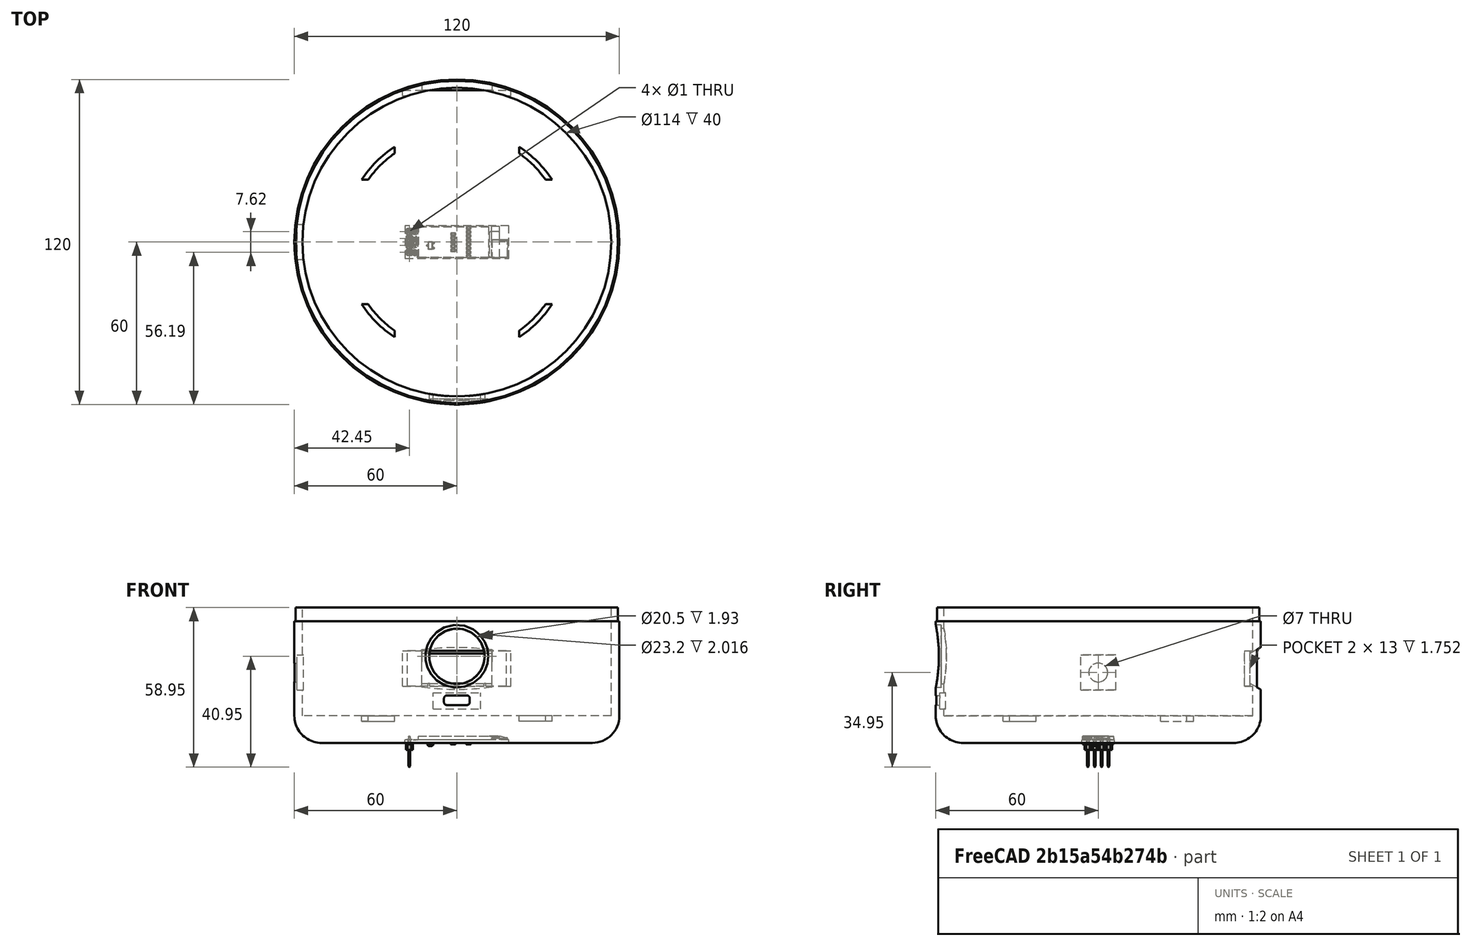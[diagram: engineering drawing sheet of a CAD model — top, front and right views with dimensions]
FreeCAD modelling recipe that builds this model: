
FCSTD DOCUMENT  (FreeCAD 0.18R4 (GitTag))
Label: 1
License: All rights reserved
LicenseURL: http://en.wikipedia.org/wiki/All_rights_reserved
objects: Part::Cut×18, Part::Feature×16, Part::Box×11, Part::Cylinder×10, Part::Fillet×2, Part::Fuse×2, App::Part×1
note: 59 computed .brp shape members not serialized (recipe doc carries the construction recipe); baked Part::Feature solids carry a one-line shape summary decoded from their .brp

FEATURE [Part::Cylinder] Cylinder  label="Base"
  Angle = 360
  AttacherType = Attacher::AttachEngine3D
  Height = 50
  Radius = 60
FEATURE [Part::Cylinder] Cylinder001  label="Agujero interior"
  Angle = 360
  AttacherType = Attacher::AttachEngine3D
  Height = 40
  Placement = pos=(0,0,10) rot=(0,0,1;0rad)
  Radius = 57
FEATURE [Part::Cut] Cut  label="Base con agujero"
  Base = -> Cylinder
  Tool = -> Cylinder001
FEATURE [Part::Fillet] Fillet  label="Curva base"
  Base = -> Cut
  Edges = 1 edges r=10: [Edge3]
FEATURE [Part::Cylinder] Cylinder002  label="Cilindro"
  Angle = 360
  AttacherType = Attacher::AttachEngine3D
  Height = 10
  Radius = 60
FEATURE [Part::Cylinder] Cylinder003  label="Cilindro001"
  Angle = 360
  AttacherType = Attacher::AttachEngine3D
  Height = 10
  Radius = 59.5
FEATURE [Part::Cut] Cut001  label="Corte para radio fino"
  Base = -> Cylinder002
  Placement = pos=(0,0,45) rot=(0,0,1;0rad)
  Tool = -> Cylinder003
FEATURE [Part::Cut] Cut002  label="Base001"
  Base = -> Fillet
  Tool = -> Cut001
FEATURE [Part::Box] Box  label="USBC"
  AttacherType = Attacher::AttachEngine3D
  Height = 3.5
  Length = 9.5
  Placement = pos=(-4.75,-100,4) rot=(0,0,1;0rad)
  Width = 10
FEATURE [Part::Fillet] Fillet001  label="USBC001"
  Base = -> Box
  Edges = 4 edges r=1: [Edge2,Edge4,Edge6,Edge8]
  Placement = pos=(0,36,10) rot=(0,0,1;0rad)
FEATURE [Part::Cut] Cut003  label="Corte USB"
  Base = -> Cut002
  Tool = -> Fillet001
FEATURE [Part::Cylinder] Cylinder004  label="Botón encendido"
  Angle = 360
  AttacherType = Attacher::AttachEngine3D
  Height = 20
  Placement = pos=(0,-51,32) rot=(1,0,0;1.5708rad)
  Radius = 10.25
FEATURE [Part::Cut] Cut004  label="Corte con boton"
  Base = -> Cut003
  Tool = -> Cylinder004
FEATURE [Part::Cylinder] Cylinder005  label="Botón encendido hueco"
  Angle = 360
  AttacherType = Attacher::AttachEngine3D
  Height = 20
  Placement = pos=(0,-58,32) rot=(1,0,0;1.5708rad)
  Radius = 11.6
FEATURE [Part::Cut] Cut005
  Base = -> Cut004
  Tool = -> Cylinder005
FEATURE [Part::Box] Box001  label="Hueco USBC"
  AttacherType = Attacher::AttachEngine3D
  Height = 6
  Length = 17.5
  Placement = pos=(-8.75,-58.5,12.5) rot=(0,0,1;0rad)
  Width = 10
FEATURE [Part::Cut] Cut006
  Base = -> Cut005
  Tool = -> Box001
FEATURE [Part::Feature] Part__Feature  label="OLED_0.91_128x32"
  shape: bbox 38.3 x 12.1 x 2.57 mm, 270 faces (baked)
FEATURE [Part::Feature] Part__Feature001  label="Pin Header 4 x 1 TH 2.54mm Pitch"
  Placement = pos=(-17.55,-3.81,-2.6) rot=(0,0,1;0rad)
  shape: bbox 2.54 x 10.16 x 11.43 mm, 136 faces, 8 solids (baked)
FEATURE [Part::Feature] Part__Feature002  label="RESC-0603"
  Placement = pos=(4.3,-5.3,2e-15) rot=(1,0,0;3.14159rad)
  shape: bbox 1.7 x 0.9 x 0.55 mm, 52 faces, 3 solids (baked)
FEATURE [Part::Feature] Part__Feature003  label="RESC-0604"
  Placement = pos=(4.3,-3.8,2e-15) rot=(1,0,0;3.14159rad)
  shape: bbox 1.7 x 0.9 x 0.55 mm, 52 faces, 3 solids (baked)
FEATURE [Part::Feature] Part__Feature004  label="RESC-0605"
  Placement = pos=(4.3,-2.3,2e-15) rot=(1,0,0;3.14159rad)
  shape: bbox 1.7 x 0.9 x 0.55 mm, 52 faces, 3 solids (baked)
FEATURE [Part::Feature] Part__Feature005  label="RESC-0606"
  Placement = pos=(4.3,-0.8,2e-15) rot=(1,0,0;3.14159rad)
  shape: bbox 1.7 x 0.9 x 0.55 mm, 52 faces, 3 solids (baked)
FEATURE [Part::Feature] Part__Feature006  label="RESC-0607"
  Placement = pos=(4.3,0.7,2e-15) rot=(1,0,0;3.14159rad)
  shape: bbox 1.7 x 0.9 x 0.55 mm, 52 faces, 3 solids (baked)
FEATURE [Part::Feature] Part__Feature007  label="RESC-0608"
  Placement = pos=(4.3,2.2,2e-15) rot=(1,0,0;3.14159rad)
  shape: bbox 1.7 x 0.9 x 0.55 mm, 52 faces, 3 solids (baked)
FEATURE [Part::Feature] Part__Feature008  label="RESC-0609"
  Placement = pos=(4.3,3.7,2e-15) rot=(1,0,0;3.14159rad)
  shape: bbox 1.7 x 0.9 x 0.55 mm, 52 faces, 3 solids (baked)
FEATURE [Part::Feature] Part__Feature009  label="RESC-0610"
  Placement = pos=(4.3,5.2,2e-15) rot=(1,0,0;3.14159rad)
  shape: bbox 1.7 x 0.9 x 0.55 mm, 52 faces, 3 solids (baked)
FEATURE [Part::Feature] Part__Feature010  label="RESC-0611"
  Placement = pos=(-1.4,-3.06,2e-15) rot=(1,0,0;3.14159rad)
  shape: bbox 1.7 x 0.9 x 0.55 mm, 52 faces, 3 solids (baked)
FEATURE [Part::Feature] Part__Feature011  label="RESC-0612"
  Placement = pos=(-1.4,-1.56,2e-15) rot=(1,0,0;3.14159rad)
  shape: bbox 1.7 x 0.9 x 0.55 mm, 52 faces, 3 solids (baked)
FEATURE [Part::Feature] Part__Feature012  label="RESC-0613"
  Placement = pos=(-1.4,-0.06,2e-15) rot=(1,0,0;3.14159rad)
  shape: bbox 1.7 x 0.9 x 0.55 mm, 52 faces, 3 solids (baked)
FEATURE [Part::Feature] Part__Feature013  label="RESC-0614"
  Placement = pos=(-1.4,1.44,2e-15) rot=(1,0,0;3.14159rad)
  shape: bbox 1.7 x 0.9 x 0.55 mm, 52 faces, 3 solids (baked)
FEATURE [Part::Feature] Part__Feature014  label="RESC-0615"
  Placement = pos=(-1.4,2.94,2e-15) rot=(1,0,0;3.14159rad)
  shape: bbox 1.7 x 0.9 x 0.55 mm, 52 faces, 3 solids (baked)
FEATURE [Part::Feature] Part__Feature015  label="2SD0601A"
  Placement = pos=(-9.8,-1.3,-0.08) rot=(-1,0,0;1.5708rad)
  shape: bbox 2.759 x 2.9 x 1.18 mm, 55 faces, 4 solids (baked)
FEATURE [App::Part] OLED_0_91_128x32  label="OLED_0.91_128x033"
  Group = -> [Part__Feature,Part__Feature001,Part__Feature002,Part__Feature003,Part__Feature004,Part__Feature005,Part__Feature006,Part__Feature007,Part__Feature008,Part__Feature009,Part__Feature010,Part__Feature011,Part__Feature012,Part__Feature013,Part__Feature014,Part__Feature015]
  Origin = -> Origin
  Placement = pos=(-1.3,54,27.5) rot=(0,-0.707107,-0.707107;3.14159rad)
FEATURE [Part::Box] Box002  label="Pantalla"
  AttacherType = Attacher::AttachEngine3D
  Height = 11
  Length = 26
  Placement = pos=(-13,55,22) rot=(0,0,1;0rad)
  Width = 9
FEATURE [Part::Box] Box003  label="Hueco pantalla"
  AttacherType = Attacher::AttachEngine3D
  Height = 13
  Length = 40
  Placement = pos=(-20,54,21) rot=(0,0,1;0rad)
  Width = 2
FEATURE [Part::Cut] Cut007
  Base = -> Cut006
  Tool = -> Box002
FEATURE [Part::Cut] Cut008
  Base = -> Cut007
  Tool = -> Box003
FEATURE [Part::Box] Box007  label="Cubo"
  AttacherType = Attacher::AttachEngine3D
  Height = 1
  Length = 20
  Placement = pos=(-10,56,21) rot=(0,0,1;0rad)
  Width = 3
FEATURE [Part::Box] Box008  label="Cubo005"
  AttacherType = Attacher::AttachEngine3D
  Height = 1
  Length = 20
  Placement = pos=(-10,56,33) rot=(0,0,1;0rad)
  Width = 3
FEATURE [Part::Fuse] Fusion
  Base = -> Cut008
  Tool = -> Box007
FEATURE [Part::Fuse] Fusion001
  Base = -> Box008
  Tool = -> Fusion
FEATURE [Part::Cylinder] Cylinder006  label="Base002"
  Angle = 360
  AttacherType = Attacher::AttachEngine3D
  Height = 154
  Placement = pos=(0,0,-2) rot=(0,0,1;0rad)
  Radius = 42
FEATURE [Part::Cylinder] Cylinder007  label="Agujero superior"
  Angle = 360
  AttacherType = Attacher::AttachEngine3D
  Height = 15
  Placement = pos=(0,0,138) rot=(0,0,1;0rad)
  Radius = 19.5
FEATURE [Part::Cylinder] Cylinder008  label="Agujero inferior"
  Angle = 360
  AttacherType = Attacher::AttachEngine3D
  Height = 138
  Placement = pos=(0,0,-2) rot=(0,0,1;0rad)
  Radius = 40
FEATURE [Part::Box] Box009  label="Cubo006"
  AttacherType = Attacher::AttachEngine3D
  Height = 138
  Length = 46
  Placement = pos=(-23,-50,-2) rot=(0,0,1;0rad)
  Width = 99
FEATURE [Part::Box] Box010  label="Cubo001"
  AttacherType = Attacher::AttachEngine3D
  Height = 138
  Length = 46
  Placement = pos=(44,-23,-2) rot=(0,0,1;1.5708rad)
  Width = 99
FEATURE [Part::Cut] Cut009  label="Corte superior"
  Base = -> Cylinder006
  Tool = -> Cylinder007
FEATURE [Part::Cut] Cut011  label="Corte inferior"
  Base = -> Cut009
  Tool = -> Cylinder008
FEATURE [Part::Cut] Cut010
  Base = -> Cut011
  Tool = -> Box009
FEATURE [Part::Cut] Cut012
  Base = -> Cut010
  Placement = pos=(0,0,10) rot=(0,0,1;0rad)
  Tool = -> Box010
FEATURE [Part::Cut] Cut013
  Base = -> Fusion001
  Tool = -> Cut012
FEATURE [Part::Box] Box011  label="Cubo007"
  AttacherType = Attacher::AttachEngine3D
  Height = 10
  Length = 26
  Placement = pos=(-13,64.66,17) rot=(1,0,0;1.0472rad)
  Width = 10
FEATURE [Part::Cut] Cut014
  Base = -> Cut013
  Tool = -> Box011
FEATURE [Part::Box] Box012  label="Cubo008"
  AttacherType = Attacher::AttachEngine3D
  Height = 10
  Length = 26
  Placement = pos=(13,64.66,38) rot=(0,0.866025,-0.5;3.14159rad)
  Width = 10
FEATURE [Part::Cut] Cut015
  Base = -> Cut014
  Tool = -> Box012
FEATURE [Part::Cylinder] Cylinder009  label="Cilindro002"
  Angle = 360
  AttacherType = Attacher::AttachEngine3D
  Height = 19
  Placement = pos=(-71,0,26) rot=(0,1,0;1.5708rad)
  Radius = 3.5
FEATURE [Part::Cut] Cut016
  Base = -> Cut015
  Tool = -> Cylinder009
FEATURE [Part::Box] Box013  label="Cubo009"
  AttacherType = Attacher::AttachEngine3D
  Height = 13
  Length = 13
  Placement = pos=(-59,-6.5,19.5) rot=(0,0,1;0rad)
  Width = 13
FEATURE [Part::Cut] Cut017
  Base = -> Cut016
  Tool = -> Box013
